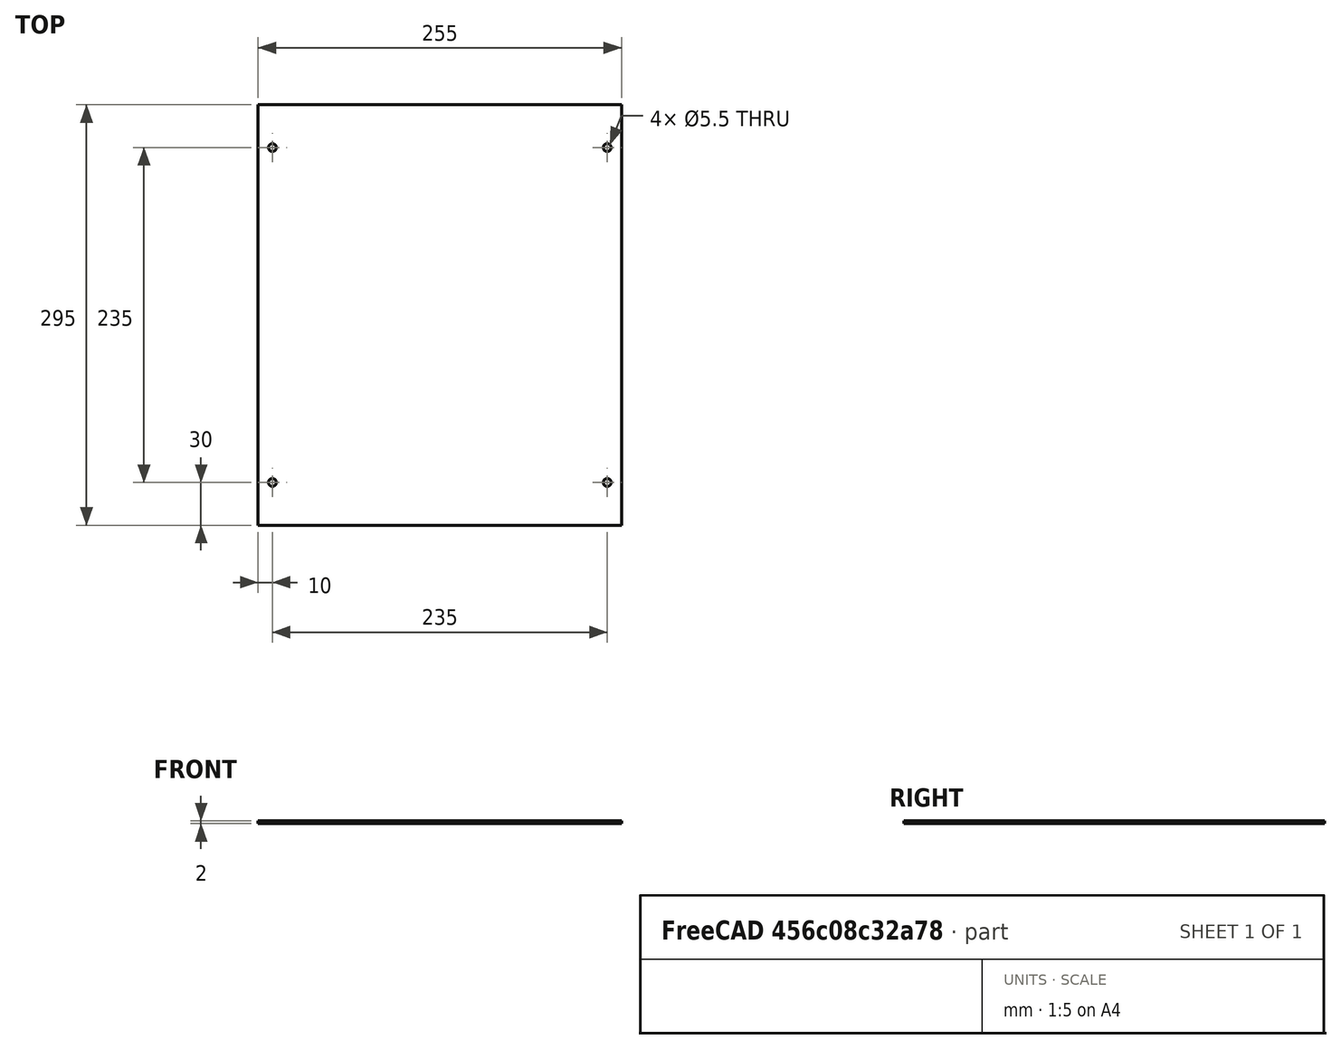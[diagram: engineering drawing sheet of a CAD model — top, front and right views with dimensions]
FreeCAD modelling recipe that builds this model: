
FCSTD DOCUMENT  (FreeCAD 0.17R13509 (Git))
Label: OCLab
License: All rights reserved
LicenseURL: http://en.wikipedia.org/wiki/All_rights_reserved
objects: TechDraw::DrawViewDimension×5, Part::Cylinder×4, Part::Cut×4, Part::Box×1, TechDraw::DrawSVGTemplate×1, TechDraw::DrawViewPart×1, TechDraw::DrawPage×1
note: 9 computed .brp shape members not serialized (recipe doc carries the construction recipe); baked Part::Feature solids carry a one-line shape summary decoded from their .brp

FEATURE [Part::Box] Box  label="Cube"
  AttacherType = Attacher::AttachEngine3D
  Height = 2
  Length = 255
  Placement = pos=(0,0,1.5332e-08) rot=(0,0,1;0rad)
  Width = 295
FEATURE [Part::Cylinder] Cylinder
  Angle = 360
  AttacherType = Attacher::AttachEngine3D
  Height = 10
  Placement = pos=(10,30,-5) rot=(0,0,1;0rad)
  Radius = 2.75
FEATURE [Part::Cylinder] Cylinder001
  Angle = 360
  AttacherType = Attacher::AttachEngine3D
  Height = 10
  Placement = pos=(10,265,-5) rot=(0,0,1;0rad)
  Radius = 2.75
FEATURE [Part::Cylinder] Cylinder002
  Angle = 360
  AttacherType = Attacher::AttachEngine3D
  Height = 10
  Placement = pos=(245,30,-5) rot=(0,0,1;0rad)
  Radius = 2.75
FEATURE [Part::Cylinder] Cylinder003
  Angle = 360
  AttacherType = Attacher::AttachEngine3D
  Height = 10
  Placement = pos=(245,265,-5) rot=(0,0,1;0rad)
  Radius = 2.75
FEATURE [Part::Cut] Cut
  Base = -> Box
  Tool = -> Cylinder
FEATURE [Part::Cut] Cut001
  Base = -> Cut
  Tool = -> Cylinder001
FEATURE [Part::Cut] Cut002
  Base = -> Cut001
  Tool = -> Cylinder002
FEATURE [Part::Cut] Cut003  label="bottom"
  Base = -> Cut002
  Tool = -> Cylinder003
FEATURE [TechDraw::DrawSVGTemplate] Template
  EditableTexts = Designed_by_Name=Fichou Dimitri; FC-Date=20180409; FC-SC=0.33; FC-Title=OCLab; Subtitle=Bottom frame
  Height = 210
  Orientation = 1
  Width = 297
FEATURE [TechDraw::DrawViewPart] View
  CoarseView = false
  Direction = (0,0,1)
  Focus = 100
  HardHidden = false
  IsoCount = 0
  IsoHidden = false
  IsoVisible = false
  LockPosition = false
  Perspective = false
  Rotation = 90
  Scale = 0.33
  ScaleType = 1
  SeamHidden = false
  SeamVisible = false
  SmoothHidden = false
  SmoothVisible = false
  Source = -> [Cut003]
  X = 155.029
  Y = 125.7
FEATURE [TechDraw::DrawViewDimension] Dimension
  FormatSpec = %.2f
  LockPosition = false
  MeasureType = 1
  References2D = -> [View]
  Rotation = 0
  ScaleType = 0
  Type = 2
  X = -67.5913
  Y = -3.4137
FEATURE [TechDraw::DrawViewDimension] Dimension001
  FormatSpec = %.2f
  LockPosition = false
  MeasureType = 1
  References2D = -> [View]
  Rotation = 0
  ScaleType = 0
  Type = 1
  X = -3.23095
  Y = 58.4802
FEATURE [TechDraw::DrawViewDimension] Dimension002
  FormatSpec = %.2f
  LockPosition = false
  MeasureType = 1
  References2D = -> [View]
  Rotation = 0
  ScaleType = 0
  Type = 5
  X = 87.0997
  Y = 2.02557
FEATURE [TechDraw::DrawViewDimension] Dimension003
  FormatSpec = %.2f
  LockPosition = false
  MeasureType = 1
  References2D = -> [View]
  Rotation = 0
  ScaleType = 0
  Type = 1
  X = 70.858
  Y = -53.7895
FEATURE [TechDraw::DrawViewDimension] Dimension004
  FormatSpec = %.2f
  LockPosition = false
  MeasureType = 1
  References2D = -> [View]
  Rotation = 0
  ScaleType = 0
  Type = 2
  X = 71.8584
  Y = -28.163
FEATURE [TechDraw::DrawPage] Page
  KeepUpdated = true
  ProjectionType = 0
  Template = -> Template
  Views = -> [View,Dimension,Dimension001,Dimension002,Dimension003,Dimension004]
